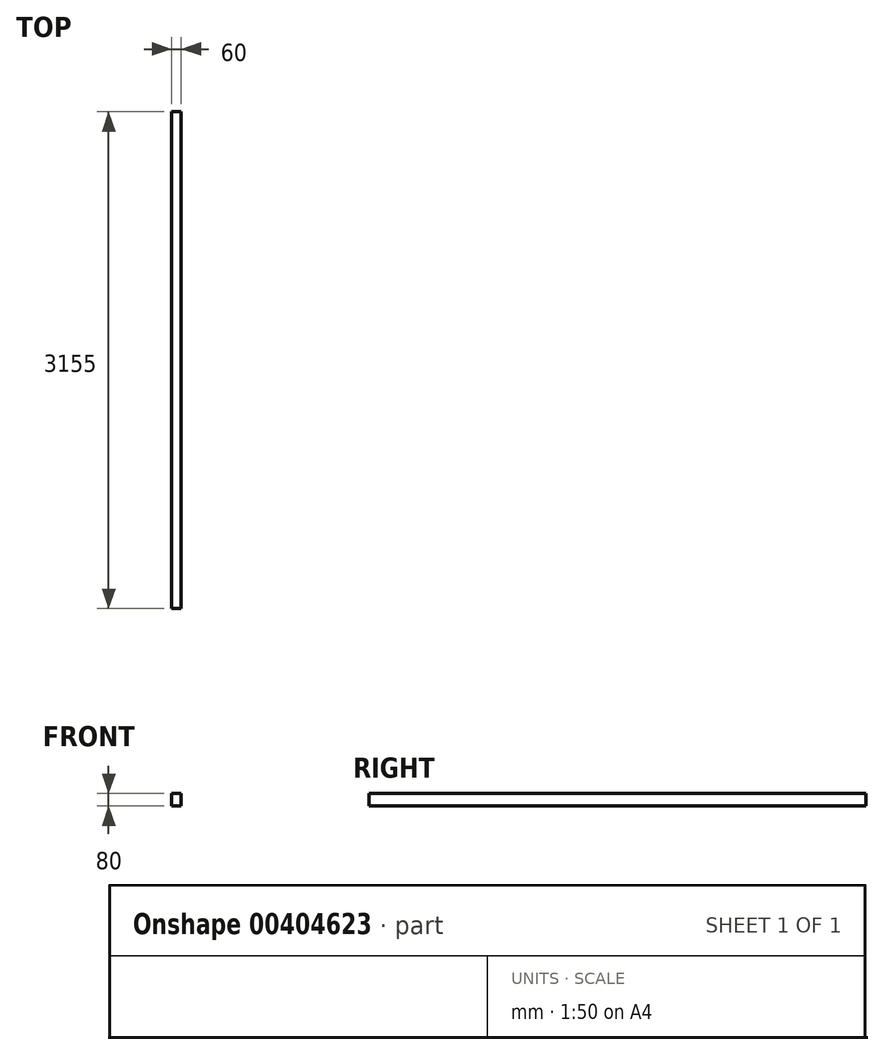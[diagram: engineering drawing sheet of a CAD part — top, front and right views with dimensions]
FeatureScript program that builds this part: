
annotation { "Feature Type Name" : "Feature", "Feature Type Description" : "" }
export const myFeature = defineFeature(function(context is Context, id is Id, definition is map)
    precondition{}
    {
        {
            var Q0;
            Q0=qCreatedBy(makeId("Front.planeOp"),FACE);
            var sketch = newSketch(context, id + "F0", { "sketchPlane" : qUnion([Q0])});
            skLineSegment(sketch, "E0.bottom", {"start": v(-30, 40) * mm, "end": v(30, 40) * mm});
            skLineSegment(sketch, "E0.top", {"start": v(-30, -40) * mm, "end": v(30, -40) * mm});
            skLineSegment(sketch, "E0.left", {"start": v(-30, 40) * mm, "end": v(-30, -40) * mm});
            skLineSegment(sketch, "E0.right", {"start": v(30, 40) * mm, "end": v(30, -40) * mm});
            skSolve(sketch);
        }
        {
            var Q0;
            Q0=qSketchRegion(id+"F0",true);
            extrude(context, id + "F1", {"entities" : qUnion([Q0]), "depth" : 3155 * mm});
        }
    });
